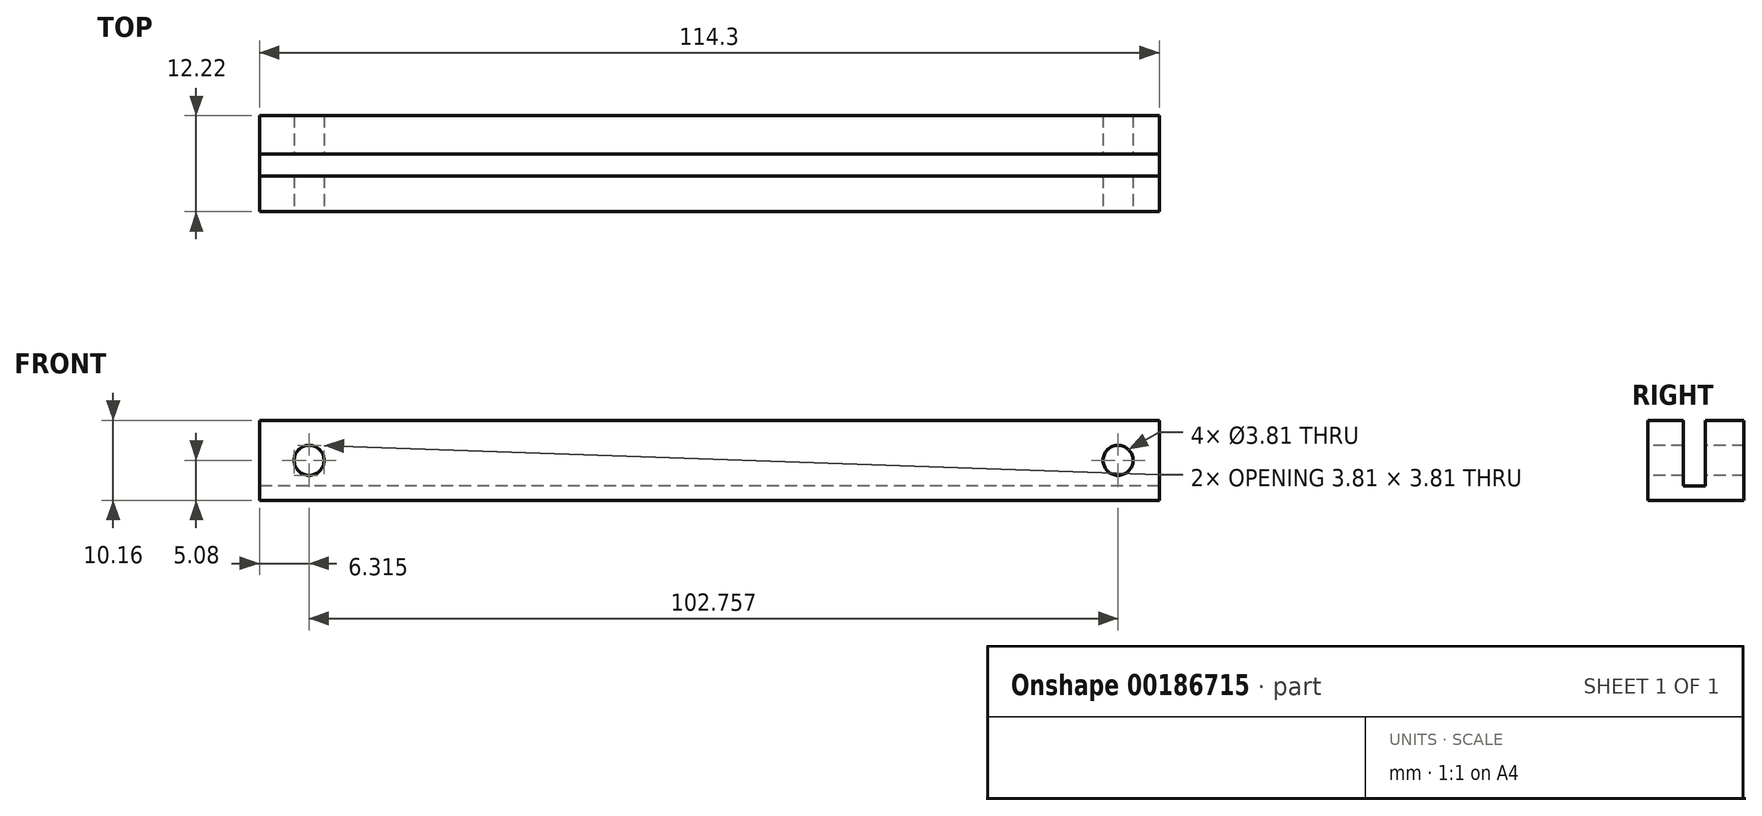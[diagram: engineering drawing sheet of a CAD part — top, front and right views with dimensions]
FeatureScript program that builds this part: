
annotation { "Feature Type Name" : "Feature", "Feature Type Description" : "" }
export const myFeature = defineFeature(function(context is Context, id is Id, definition is map)
    precondition{}
    {
        {
            var Q0;
            Q0=qCreatedBy(makeId("Front.planeOp"),FACE);
            var sketch = newSketch(context, id + "F0", { "sketchPlane" : qUnion([Q0])});
            skLineSegment(sketch, "E0.bottom", {"start": v(57.15, 5.08) * mm, "end": v(-57.15, 5.08) * mm});
            skLineSegment(sketch, "E0.top", {"start": v(57.15, -5.08) * mm, "end": v(-57.15, -5.08) * mm});
            skLineSegment(sketch, "E0.left", {"start": v(57.15, 5.08) * mm, "end": v(57.15, -5.08) * mm});
            skLineSegment(sketch, "E0.right", {"start": v(-57.15, 5.08) * mm, "end": v(-57.15, -5.08) * mm});
            skPoint(sketch, "E0.middle", {"position": v(0, 0) * mm});
            skSolve(sketch);
        }
        {
            var Q0;
            Q0 = qSketchRegion(id + "F0", true);
            extrude(context, id + "F1", {"entities" : qUnion([Q0]), "depth" : 12.22 * mm});
        }
        {
            var Q0;
            Q0=makeQuery(id+"F1.opExtrude","SWEPT_FACE",FACE,{"disambiguationData":[OSD([sQuery(id+"F0.wireOp",EDGE,"E0.bottom")])]});
            var sketch = newSketch(context, id + "F2", { "sketchPlane" : qUnion([Q0])});
            skLineSegment(sketch, "E1.bottom", {"start": v(57.15, -4.9) * mm, "end": v(-57.15, -4.9) * mm});
            skLineSegment(sketch, "E1.top", {"start": v(57.15, -7.7) * mm, "end": v(-57.15, -7.7) * mm});
            skLineSegment(sketch, "E1.left", {"start": v(57.15, -4.9) * mm, "end": v(57.15, -7.7) * mm});
            skLineSegment(sketch, "E1.right", {"start": v(-57.15, -4.9) * mm, "end": v(-57.15, -7.7) * mm});
            skPoint(sketch, "E1.middle", {"position": v(0, -6.3) * mm});
            skSolve(sketch);
        }
        {
            var Q0;
            Q0 = qSketchRegion(id + "F2", true);
            extrude(context, id + "F3", {"entities" : qUnion([Q0]), "operationType" : NewBodyOperationType.REMOVE, "oppositeDirection" : true, "depth" : 8.36 * mm});
        }
        {
            var Q0;
            Q0=makeQuery(id+"F1.opExtrude","CAP_FACE",FACE,{"disambiguationData":[OSD([sQuery(id+"F0.wireOp",EDGE,"E0.bottom"),sQuery(id+"F0.wireOp",EDGE,"E0.top"),sQuery(id+"F0.wireOp",EDGE,"E0.left"),sQuery(id+"F0.wireOp",EDGE,"E0.right")])],"isStart":false});
            var sketch = newSketch(context, id + "F4", { "sketchPlane" : qUnion([Q0])});
            skCircle(sketch, "E2", {"center": v(-50.84, 0) * mm, "radius": 1.9 * mm});
            skPoint(sketch, "E2.centerSnap0", {"position": v(-57.15, 0) * mm});
            skCircle(sketch, "E3", {"center": v(51.92, 0) * mm, "radius": 1.9 * mm});
            skPoint(sketch, "E3.centerSnap0", {"position": v(57.15, 0) * mm});
            skSolve(sketch);
        }
        {
            var Q0;
            Q0 = qSketchRegion(id + "F4", true);
            extrude(context, id + "F5", {"entities" : qUnion([Q0]), "operationType" : NewBodyOperationType.REMOVE, "oppositeDirection" : true, "depth" : 25.4 * mm});
        }
    });
